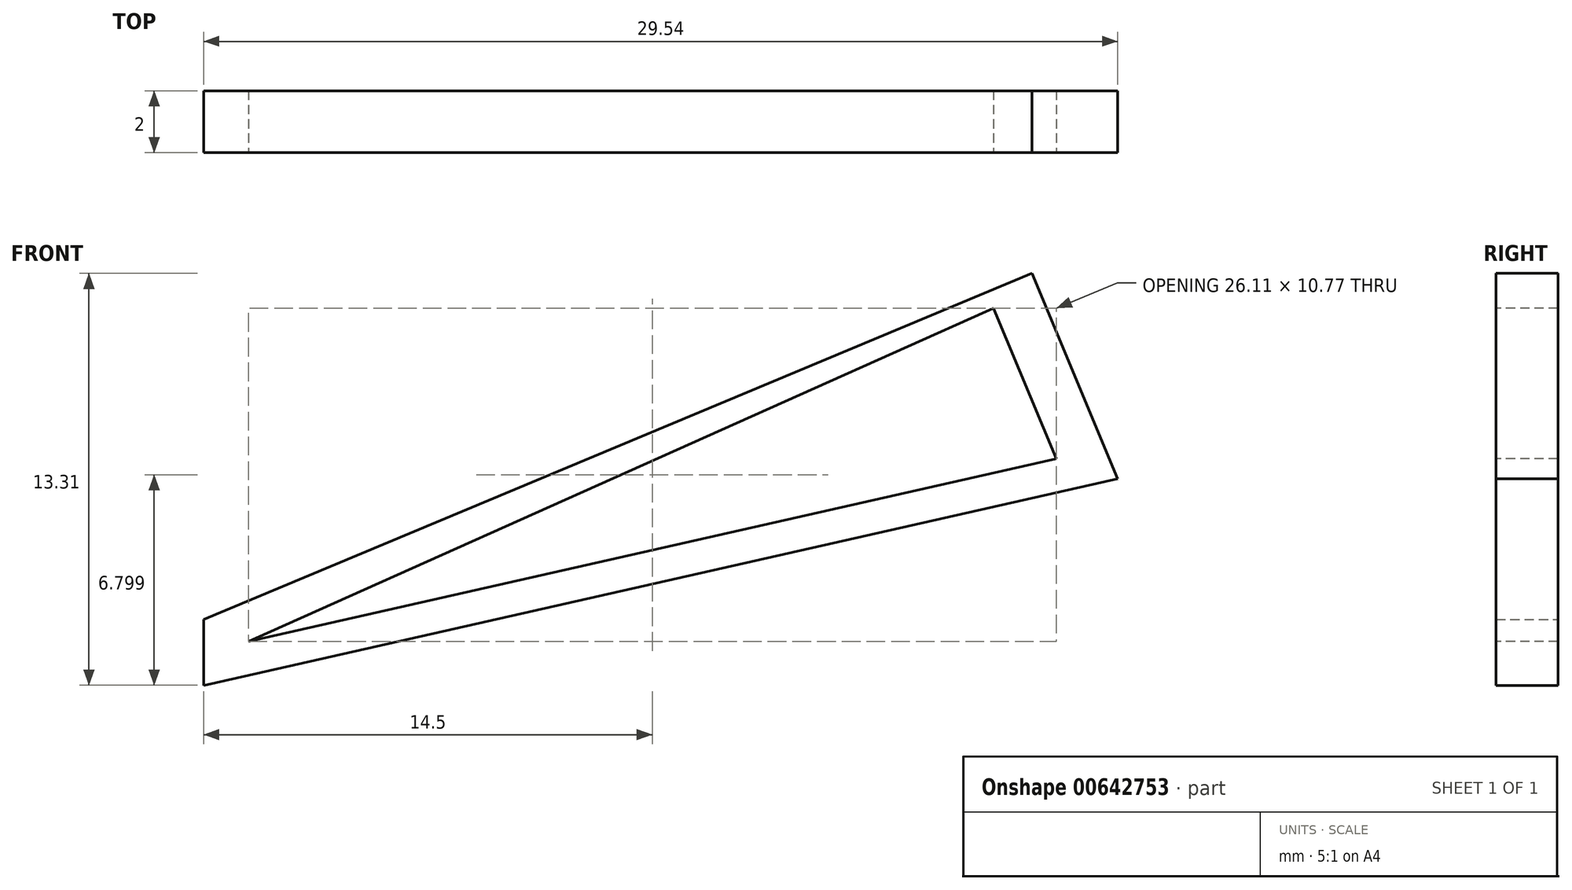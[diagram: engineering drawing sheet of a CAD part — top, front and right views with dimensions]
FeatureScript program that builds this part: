
annotation { "Feature Type Name" : "Feature", "Feature Type Description" : "" }
export const myFeature = defineFeature(function(context is Context, id is Id, definition is map)
    precondition{}
    {
        {
            var Q0;
            Q0=qCreatedBy(makeId("Front.planeOp"),FACE);
            var sketch = newSketch(context, id + "F0", { "sketchPlane" : qUnion([Q0])});
            skLineSegment(sketch, "E0", {"start": v(0, 0) * mm, "end": v(26.77, 11.19) * mm});
            skLineSegment(sketch, "E1", {"start": v(26.77, 11.19) * mm, "end": v(29.54, 4.56) * mm});
            skLineSegment(sketch, "E2", {"start": v(29.54, 4.56) * mm, "end": v(0, -2.12) * mm});
            skLineSegment(sketch, "E3", {"start": v(0, 0) * mm, "end": v(0, -2.12) * mm});
            skSolve(sketch);
        }
        {
            var Q0;
            Q0 = qSketchRegion(id + "F0", true);
            extrude(context, id + "F1", {"entities" : qUnion([Q0]), "depth" : 2 * mm, "offsetDistance" : 25 * mm});
        }
        {
            var Q0;
            Q0=makeQuery(id+"F1.opExtrude","CAP_FACE",FACE,{"disambiguationData":[OSD([sQuery(id+"F0.wireOp",EDGE,"E0"),sQuery(id+"F0.wireOp",EDGE,"E1"),sQuery(id+"F0.wireOp",EDGE,"E2"),sQuery(id+"F0.wireOp",EDGE,"E3")])],"isStart":false});
            var sketch = newSketch(context, id + "F2", { "sketchPlane" : qUnion([Q0])});
            skLineSegment(sketch, "E4", {"start": v(25.53, 10.06) * mm, "end": v(27.56, 5.2) * mm});
            skLineSegment(sketch, "E5", {"start": v(27.56, 5.2) * mm, "end": v(1.44, -0.7) * mm});
            skLineSegment(sketch, "E6", {"start": v(1.44, -0.7) * mm, "end": v(25.53, 10.06) * mm});
            skSolve(sketch);
        }
        {
            var Q0;
            Q0 = qSketchRegion(id + "F2", true);
            extrude(context, id + "F3", {"entities" : qUnion([Q0]), "operationType" : NewBodyOperationType.REMOVE, "endBound" : BoundingType.THROUGH_ALL, "oppositeDirection" : true, "depth" : 25 * mm, "offsetDistance" : 25 * mm});
        }
    });
